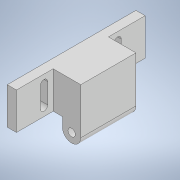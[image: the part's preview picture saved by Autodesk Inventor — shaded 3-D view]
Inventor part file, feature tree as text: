
AUTODESK INVENTOR PART (.ipt)
format: ipt  version: 2022 (Build 260153000, 153)  size: 167,936 bytes
history: native  units: in
note: dims shown in document units (in); Inventor stores cm internally (conversion verified against a paired STEP export)
features: sketch x7, extrude x6, hole x1
ambient origin geometry x8: Origin, YZ Plane, XZ Plane, XY Plane, X Axis, Y Axis, Z Axis, Center Point
bodies: Solid1 (feature_tree)
feature tree (14):
  extrude  "Extrusion1"  Depth=1.25in
  extrude  "Extrusion2"  Depth=0.5in
  extrude  "Extrusion3"  TaperAngle=0.0deg  [1 undecoded]
  extrude  "Extrusion4"  Depth=0.25in
  hole  "Hole1"  [1 undecoded]
  extrude  "Extrusion6"  Depth=0.125in
  extrude  "Extrusion7"  Depth=0.375in
  sketch  "Sketch1"  dims[d0=0.5in d1=1.25in]
  sketch  "Sketch2"  dims[d2=0.75in d3=0.0in d4=0.5in]
  sketch  "Sketch3"  dims[d5=0.125in d6=0.0in d7=0.0in]
  sketch  "Sketch4"  dims[d8=0.25in d9=0.25in]
  sketch  "Sketch6"  dims[d10=0.0in d11=0.0in d12=0.5in d13=0.0in]
  sketch  "Sketch7"  dims[d18=0.125in d19=0.125in]
  sketch  "Sketch8"  dims[d20=0.1in d21=0.75in d22=0.375in d23=0.25in d24=0.5635in d25=1.0in d26=0.8108in d27=0.275in d28=0.375in d29=0.25in d30=0.1in d31=0.1in d32=0.25in d33=0.275in d34=0.375in d35=0.0in d36=0.0in d37=0.0in d38=0.0in]
note: 2 required parameter values undecoded (feature->parameter linkage not recoverable at this tier; creation-order binding heuristic only, values carry confidence <= 0.55)
